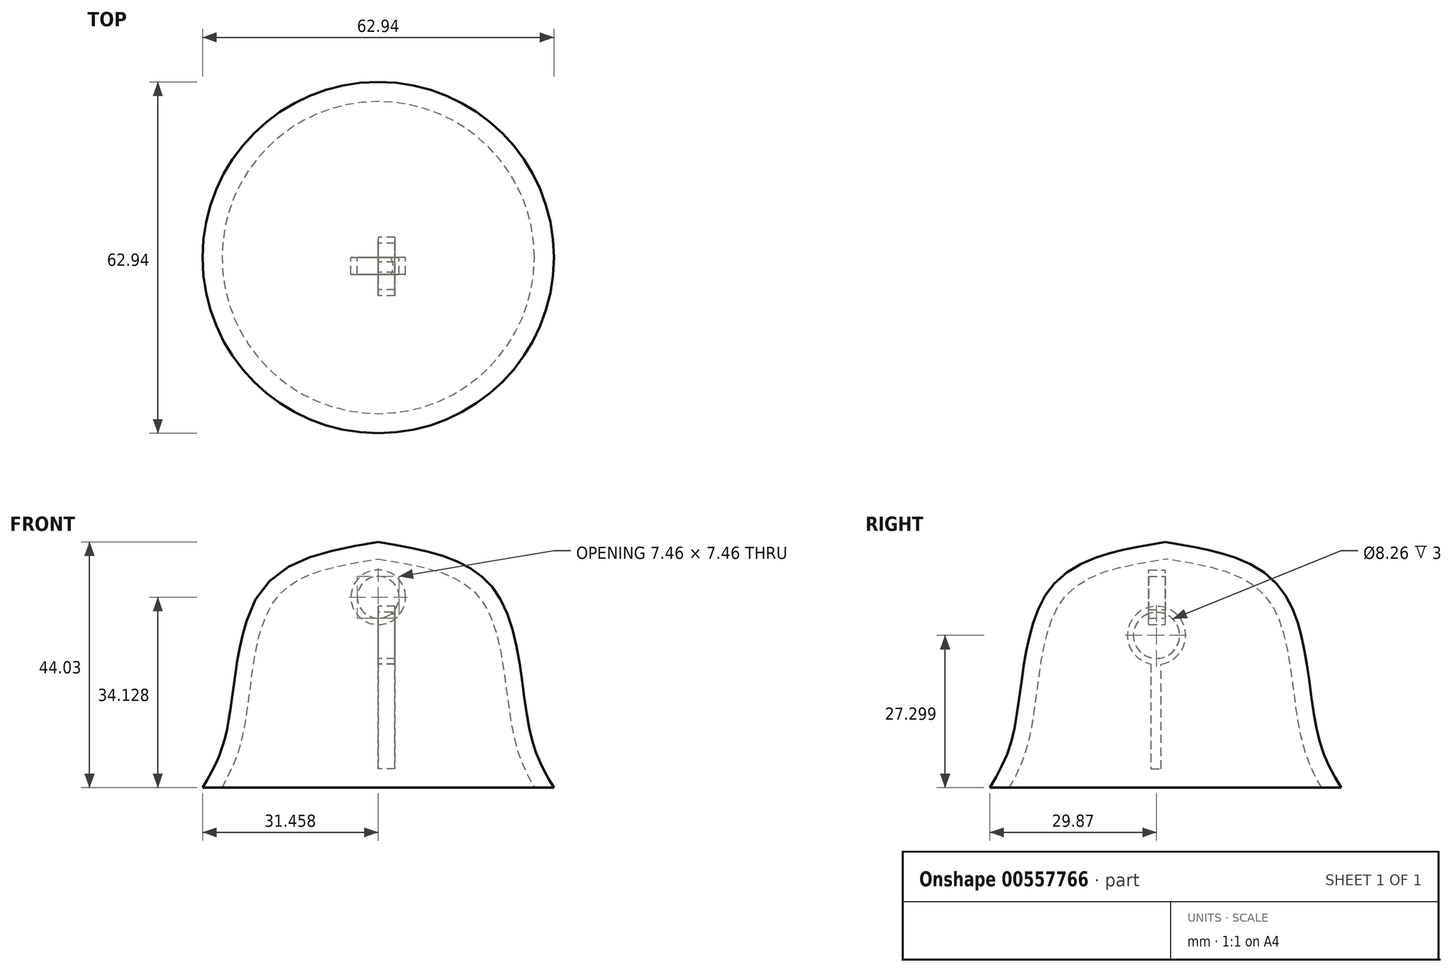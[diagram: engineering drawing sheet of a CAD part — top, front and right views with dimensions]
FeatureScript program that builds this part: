
annotation { "Feature Type Name" : "Feature", "Feature Type Description" : "" }
export const myFeature = defineFeature(function(context is Context, id is Id, definition is map)
    precondition{}
    {
        {
            var Q0;
            Q0=qCreatedBy(makeId("Front.planeOp"),FACE);
            var sketch = newSketch(context, id + "F0", { "sketchPlane" : qUnion([Q0])});
            skFitSpline(sketch, "E0", {"points": [v(0, 44.03) * mm, v(20.93, 35.34) * mm, v(27.13, 10.23) * mm, v(31.47, 0) * mm], "startDerivative": vector(69.01, -11.33) * mm, "endDerivative": vector(19.72, -32.88) * mm});
            skLineSegment(sketch, "E1", {"start": v(0, 44.03) * mm, "end": v(0, 0) * mm});
            skLineSegment(sketch, "E2", {"start": v(0, 0) * mm, "end": v(31.47, 0) * mm});
            skFitSpline(sketch, "E3.0", {"points": [v(-0.49, 41.07) * mm, v(0.95, 40.83) * mm, v(3.8, 40.36) * mm, v(7.81, 39.54) * mm, v(11.45, 38.5) * mm, v(14.05, 37.34) * mm, v(15.82, 36.24) * mm, v(17, 35.3) * mm, v(18.01, 34.26) * mm, v(18.9, 33.07) * mm, v(19.68, 31.64) * mm, v(20.61, 29.45) * mm, v(21.54, 26.27) * mm, v(22.35, 22.03) * mm, v(22.85, 18.36) * mm, v(23.23, 15.48) * mm, v(23.52, 13.37) * mm, v(23.8, 11.68) * mm, v(24.03, 10.37) * mm, v(24.23, 9.41) * mm, v(24.45, 8.5) * mm, v(24.76, 7.32) * mm, v(25.19, 5.95) * mm, v(25.75, 4.44) * mm, v(26.56, 2.6) * mm, v(27.63, 0.56) * mm, v(28.49, -0.86) * mm, v(28.9, -1.54) * mm]});
            skSolve(sketch);
        }
        {
            var Q0;
            {var subQ0=sQuery(id+"F0.wireOp",EDGE,"E0");Q0=makeQuery(id+"F0.imprint","IMPRINT",FACE,{"disambiguationData":[TD([[makeQuery(id+"F0.imprint","IMPRINT",EDGE,{"derivedFrom":subQ0}),-1.0]])]});}
            var Q1;
            Q1=sQuery(id+"F0.wireOp",EDGE,"E1");
            revolve(context, id + "F1", {"entities" : qUnion([Q0]), "axis" : qUnion([Q1]), "revolveType" : RevolveType.FULL});
        }
        {
            var Q0;
            Q0=qCreatedBy(makeId("Front.planeOp"),FACE);
            var sketch = newSketch(context, id + "F2", { "sketchPlane" : qUnion([Q0])});
            skCircle(sketch, "E4", {"center": v(0, 34.12) * mm, "radius": 4.9 * mm});
            skCircle(sketch, "E5", {"center": v(0, 34.12) * mm, "radius": 3.74 * mm});
            skSolve(sketch);
        }
        {
            var Q0;
            Q0=makeQuery(id+"F2.imprint","IMPRINT",FACE,{"disambiguationData":[TD([[makeQuery(id+"F2.imprint","IMPRINT",EDGE,{"derivedFrom":sQuery(id+"F2.wireOp",EDGE,"E4")}),1.0]])]});
            extrude(context, id + "F3", {"entities" : qUnion([Q0]), "operationType" : NewBodyOperationType.ADD, "depth" : 3 * mm, "offsetDistance" : 25 * mm});
        }
        {
            var Q0;
            Q0=qCreatedBy(makeId("Right.planeOp"),FACE);
            var sketch = newSketch(context, id + "F4", { "sketchPlane" : qUnion([Q0])});
            skCircle(sketch, "E6", {"center": v(-1.6, 27.3) * mm, "radius": 4.13 * mm});
            skArc(sketch, "E7", {"start": v(-0.78, 22.15) * mm, "mid": v(-1.5, 32.5) * mm, "end": v(-2.63, 22.19) * mm});
            skLineSegment(sketch, "E8", {"start": v(-2.63, 22.19) * mm, "end": v(-2.63, 3.4) * mm});
            skLineSegment(sketch, "E9", {"start": v(-2.63, 3.4) * mm, "end": v(-0.78, 3.4) * mm});
            skLineSegment(sketch, "E10", {"start": v(-0.78, 3.4) * mm, "end": v(-0.78, 22.15) * mm});
            skSolve(sketch);
        }
        {
            var Q0;
            Q0=makeQuery(id+"F4.imprint","IMPRINT",FACE,{"disambiguationData":[TD([[makeQuery(id+"F4.imprint","IMPRINT",EDGE,{"derivedFrom":sQuery(id+"F4.wireOp",EDGE,"E6")}),-1.0]])]});
            extrude(context, id + "F5", {"entities" : qUnion([Q0]), "operationType" : NewBodyOperationType.ADD, "depth" : 3 * mm, "offsetDistance" : 25 * mm});
        }
    });
